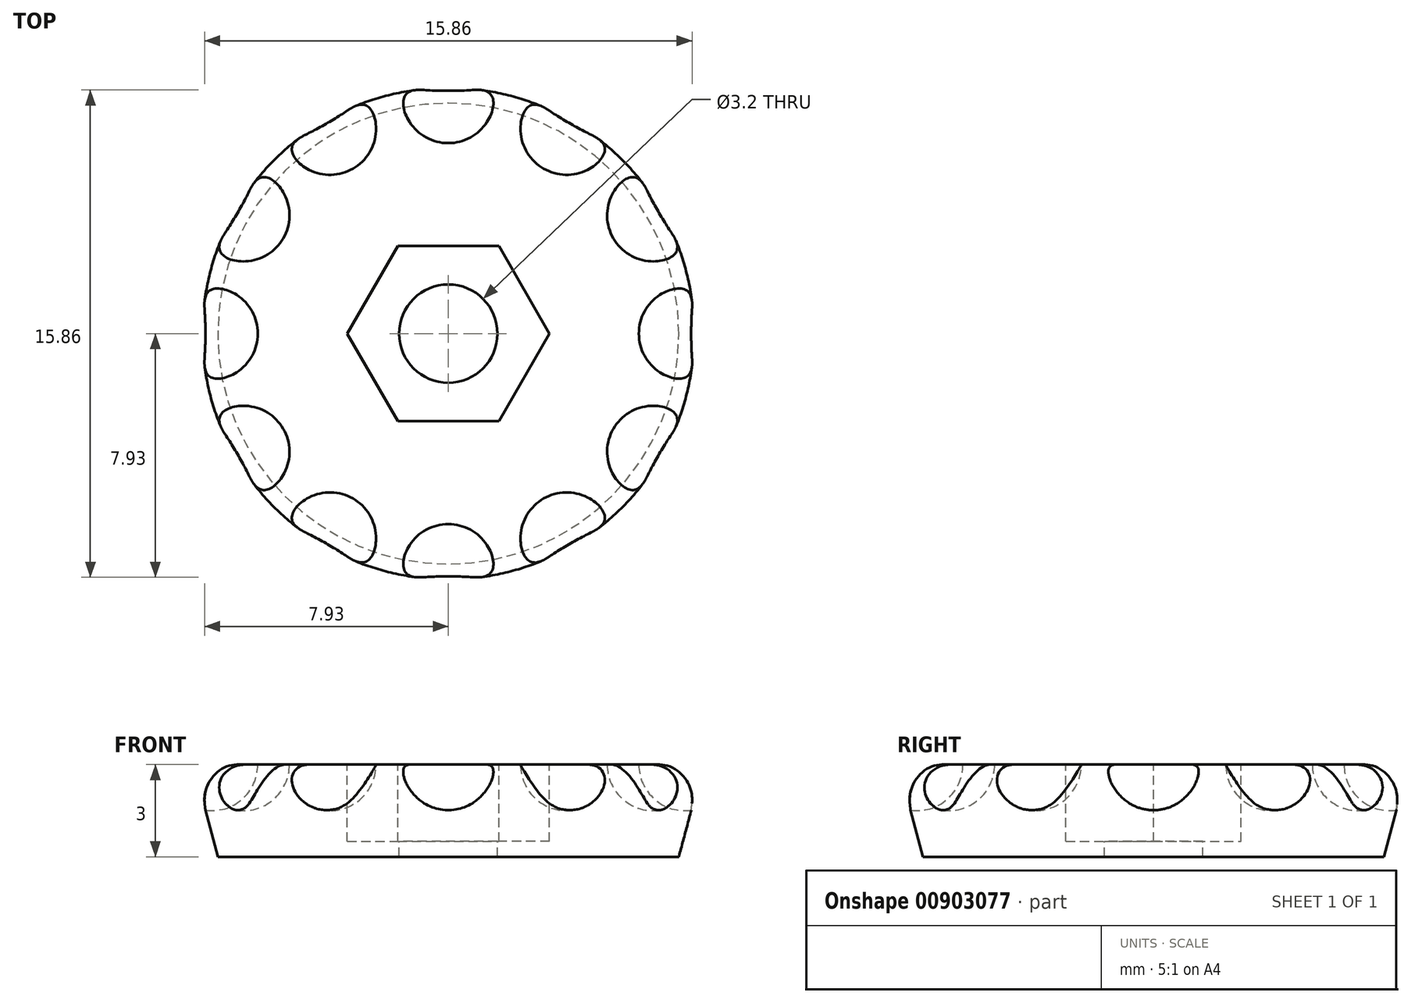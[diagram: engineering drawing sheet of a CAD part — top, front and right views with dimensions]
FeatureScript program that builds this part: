
annotation { "Feature Type Name" : "Feature", "Feature Type Description" : "" }
export const myFeature = defineFeature(function(context is Context, id is Id, definition is map)
    precondition{}
    {
        {
            var Q0;
            Q0=qCreatedBy(makeId("Top.planeOp"),FACE);
            var sketch = newSketch(context, id + "F0", { "sketchPlane" : qUnion([Q0])});
            skCircle(sketch, "E0", {"center": v(0, 0) * mm, "radius": 8.5 * mm});
            skLineSegment(sketch, "E1", {"start": v(0, 0) * mm, "end": v(0, 11.56) * mm, "construction": true});
            skSolve(sketch);
        }
        {
            var Q0;
            Q0=makeQuery(id+"F0.imprint","IMPRINT",FACE,{"disambiguationData":[TD([[makeQuery(id+"F0.imprint","IMPRINT",EDGE,{"derivedFrom":sQuery(id+"F0.wireOp",EDGE,"E0")}),1.0]])]});
            var Q1;
            Q1=sQuery(id+"F0.wireOp",EDGE,"E1");
            var Q2;
            Q2=sQuery(id+"F0.wireOp",EDGE,"E0");
            extrude(context, id + "F1", {"entities" : qUnion([Q0]), "surfaceEntities" : qUnion([Q1, Q2]), "depth" : 3 * mm, "offsetDistance" : 25 * mm});
        }
        {
            var Q0;
            Q0=makeQuery(id+"F1.opExtrude","CAP_EDGE",EDGE,{"disambiguationData":[OSD([sQuery(id+"F0.wireOp",EDGE,"E0")])],"isStart":true});
            chamfer(context, id + "F2", {"entities" : qUnion([Q0]), "chamferType" : ChamferType.OFFSET_ANGLE, "width" : 1 * mm, "oppositeDirection" : true, "angle" : 75 * degree, "tangentPropagation" : true});
        }
        {
            var Q0;
            {var subQ0=sQuery(id+"F0.wireOp",EDGE,"E0");Q0=makeQuery(id+"F2.opChamfer","BLEND_EDGE",EDGE,{"blendedFrom":[makeQuery(id+"F1.opExtrude","CAP_EDGE",EDGE,{"disambiguationData":[OSD([subQ0])],"isStart":true}),makeQuery(id+"F1.opExtrude","CAP_FACE",FACE,{"disambiguationData":[OSD([subQ0])],"isStart":false})],"blendedInto":[makeQuery(id+"F1.opExtrude","CAP_FACE",FACE,{"disambiguationData":[OSD([subQ0])],"isStart":false})]});}
            fillet(context, id + "F3", {"entities" : qUnion([Q0]), "radius" : 1 * mm, "tangentPropagation" : true, "allowEdgeOverflow" : false});
        }
        {
            var Q0;
            Q0=makeQuery(id+"F1.opExtrude","CAP_FACE",FACE,{"disambiguationData":[OSD([sQuery(id+"F0.wireOp",EDGE,"E0")])],"isStart":false});
            var sketch = newSketch(context, id + "F4", { "sketchPlane" : qUnion([Q0])});
            skArc(sketch, "E2", {"start": v(0, 6.2) * mm, "mid": v(1.5, 7.7) * mm, "end": v(0, 9.2) * mm});
            skLineSegment(sketch, "E3", {"start": v(0, 9.2) * mm, "end": v(0, 6.2) * mm});
            skPoint(sketch, "E4.orphan", {"position": v(0, 9.2) * mm});
            skCircle(sketch, "E5.0", {"center": v(0, 0) * mm, "radius": 8.5 * mm});
            skSolve(sketch);
        }
        {
            var Q0;
            {var subQ0=sQuery(id+"F4.wireOp",EDGE,"E3");var subQ1=sQuery(id+"F4.wireOp",EDGE,"E2");var subQ2=makeQuery(id+"F4.imprint","INTERSECT",VERTEX,{"disambiguationData":[OD(0.0)],"derivedFrom":[subQ1,subQ0]});Q0=makeQuery(id+"F4.imprint","IMPRINT",FACE,{"disambiguationData":[TD([[makeQuery(id+"F4.imprint","IMPRINT",EDGE,{"disambiguationData":[TD([[subQ2,-1.0]])],"derivedFrom":subQ1}),1.0]])]});}
            var Q1;
            {var subQ0=sQuery(id+"F4.wireOp",EDGE,"E3");var subQ1=sQuery(id+"F4.wireOp",EDGE,"E2");var subQ2=makeQuery(id+"F4.imprint","INTERSECT",VERTEX,{"disambiguationData":[OD(1.0)],"derivedFrom":[subQ1,subQ0]});Q1=makeQuery(id+"F4.imprint","IMPRINT",FACE,{"disambiguationData":[TD([[makeQuery(id+"F4.imprint","IMPRINT",EDGE,{"disambiguationData":[TD([[subQ2,1.0]])],"derivedFrom":subQ1}),1.0]])]});}
            var Q2;
            {var subQ0=sQuery(id+"F4.wireOp",EDGE,"E5.0");var subQ1=sQuery(id+"F4.wireOp",EDGE,"E2");var subQ2=makeQuery(id+"F4.imprint","INTERSECT",VERTEX,{"derivedFrom":[subQ1,subQ0]});Q2=makeQuery(id+"F4.imprint","IMPRINT",FACE,{"disambiguationData":[TD([[makeQuery(id+"F4.imprint","IMPRINT",EDGE,{"disambiguationData":[TD([[subQ2,-1.0]])],"derivedFrom":subQ0}),1.0]])]});}
            var Q3;
            Q3=sQuery(id+"F4.wireOp",EDGE,"E2");
            var Q4;
            Q4=sQuery(id+"F4.wireOp",EDGE,"E3");
            revolve(context, id + "F5", {"surfaceOperationType" : NewSurfaceOperationType.NEW, "entities" : qUnion([Q0, Q1, Q2]), "surfaceEntities" : qUnion([Q3]), "axis" : qUnion([Q4]), "revolveType" : RevolveType.FULL});
        }
        {
            var Q0;
            Q0=makeQuery(id+"F5.opRevolve","SWEPT_BODY",BODY,{"disambiguationData":[OSD([sQuery(id+"F4.wireOp",EDGE,"E2"),sQuery(id+"F4.wireOp",EDGE,"E3")])]});
            var Q1;
            {var subQ0=sQuery(id+"F0.wireOp",EDGE,"E0");var subQ1=makeQuery(id+"F1.opExtrude","CAP_FACE",FACE,{"disambiguationData":[OSD([subQ0])],"isStart":false});Q1=makeQuery(id+"F3.opFillet","BLEND_EDGE",EDGE,{"blendedFrom":[makeQuery(id+"F2.opChamfer","BLEND_EDGE",EDGE,{"blendedFrom":[makeQuery(id+"F1.opExtrude","CAP_EDGE",EDGE,{"disambiguationData":[OSD([subQ0])],"isStart":true}),subQ1],"blendedInto":[subQ1]}),subQ1],"blendedInto":[subQ1]});}
            circularPattern(context, id + "F6", {"operationType" : NewBodyOperationType.ADD, "entities" : qUnion([Q0]), "axis" : qUnion([Q1]), "angle" : 360 * degree, "instanceCount" : 12, "equalSpace" : true});
        }
        {
            var Q0;
            Q0=makeQuery(id+"F1.opExtrude","CAP_FACE",FACE,{"disambiguationData":[OSD([sQuery(id+"F0.wireOp",EDGE,"E0")])],"isStart":false});
            var sketch = newSketch(context, id + "F7", { "sketchPlane" : qUnion([Q0])});
            skCircle(sketch, "E6.cCircle", {"center": v(0, 0) * mm, "radius": 2.85 * mm, "construction": true});
            skLineSegment(sketch, "E6.0", {"start": v(-1.65, 2.85) * mm, "end": v(1.65, 2.85) * mm});
            skLineSegment(sketch, "E6.1", {"start": v(1.65, 2.85) * mm, "end": v(3.3, 0) * mm});
            skLineSegment(sketch, "E6.2", {"start": v(3.3, 0) * mm, "end": v(1.65, -2.85) * mm});
            skLineSegment(sketch, "E6.3", {"start": v(1.65, -2.85) * mm, "end": v(-1.65, -2.85) * mm});
            skLineSegment(sketch, "E6.4", {"start": v(-1.65, -2.85) * mm, "end": v(-3.3, 0) * mm});
            skLineSegment(sketch, "E6.5", {"start": v(-3.3, 0) * mm, "end": v(-1.65, 2.85) * mm});
            skPoint(sketch, "E6.0.midPoint", {"position": v(0, 2.85) * mm});
            skCircle(sketch, "E7", {"center": v(0, 0) * mm, "radius": 1.6 * mm});
            skSolve(sketch);
        }
        {
            var Q0;
            Q0 = qSketchRegion(id + "F7", true);
            var Q1;
            Q1=makeQuery(id+"F7.imprint","IMPRINT",FACE,{"disambiguationData":[TD([[makeQuery(id+"F7.imprint","IMPRINT",EDGE,{"derivedFrom":sQuery(id+"F7.wireOp",EDGE,"E7")}),1.0]])]});
            extrude(context, id + "F8", {"entities" : qUnion([Q0, Q1]), "operationType" : NewBodyOperationType.REMOVE, "oppositeDirection" : true, "depth" : (3 - 0.5) * mm, "offsetDistance" : 25 * mm});
        }
        {
            var Q0;
            Q0=makeQuery(id+"F7.imprint","IMPRINT",FACE,{"disambiguationData":[TD([[makeQuery(id+"F7.imprint","IMPRINT",EDGE,{"derivedFrom":sQuery(id+"F7.wireOp",EDGE,"E7")}),1.0]])]});
            var Q1;
            Q1=sQuery(id+"F7.wireOp",EDGE,"E7");
            extrude(context, id + "F9", {"entities" : qUnion([Q0]), "operationType" : NewBodyOperationType.REMOVE, "surfaceEntities" : qUnion([Q1]), "oppositeDirection" : true, "depth" : 25 * mm, "offsetDistance" : 25 * mm});
        }
    });
